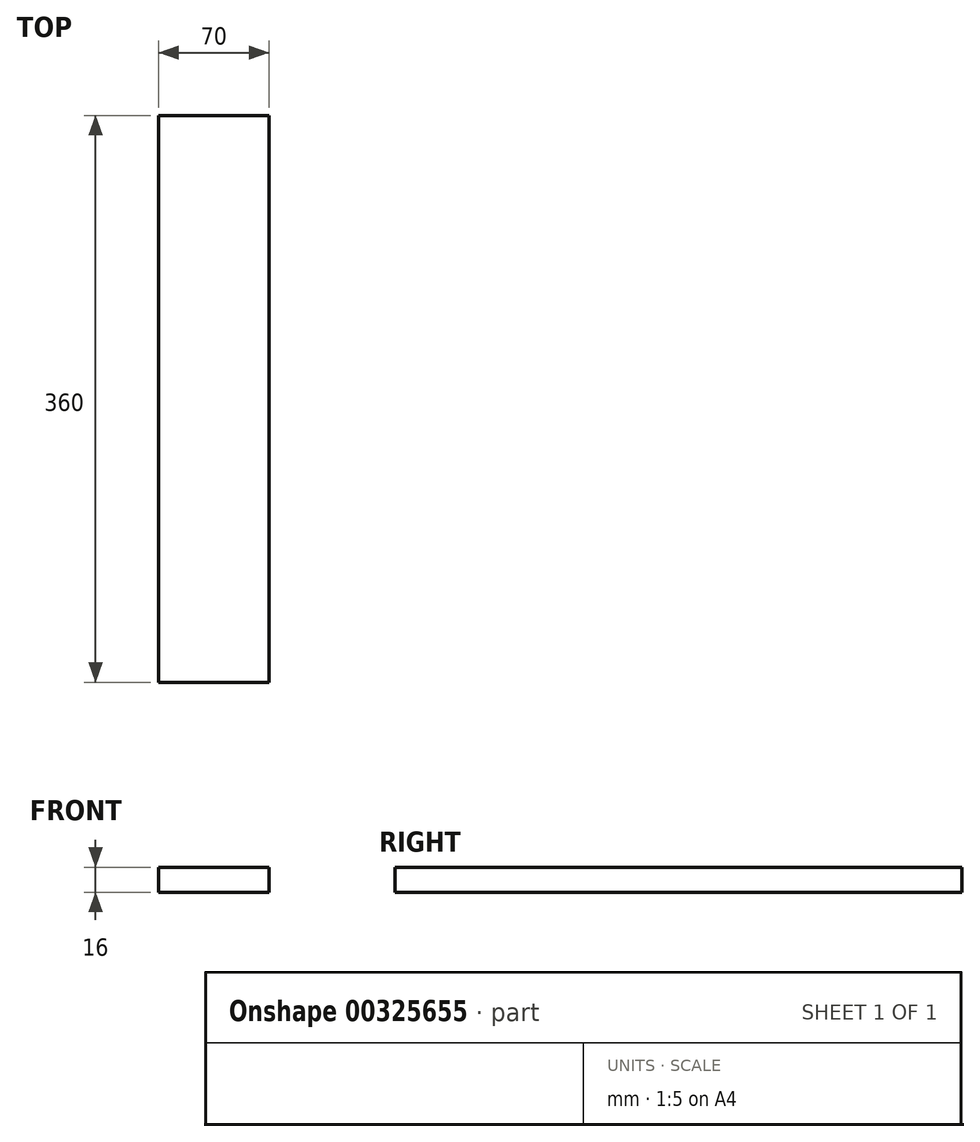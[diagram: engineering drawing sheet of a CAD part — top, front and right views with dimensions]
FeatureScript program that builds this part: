
annotation { "Feature Type Name" : "Feature", "Feature Type Description" : "" }
export const myFeature = defineFeature(function(context is Context, id is Id, definition is map)
    precondition{}
    {
        {
            var Q0;
            Q0=qCreatedBy(makeId("Front.planeOp"),FACE);
            var sketch = newSketch(context, id + "F0", { "sketchPlane" : qUnion([Q0])});
            skLineSegment(sketch, "E0.bottom", {"start": v(0, 0) * mm, "end": v(70, 0) * mm});
            skLineSegment(sketch, "E0.top", {"start": v(0, 16) * mm, "end": v(70, 16) * mm});
            skLineSegment(sketch, "E0.left", {"start": v(0, 0) * mm, "end": v(0, 16) * mm});
            skLineSegment(sketch, "E0.right", {"start": v(70, 0) * mm, "end": v(70, 16) * mm});
            skSolve(sketch);
        }
        {
            var Q0;
            Q0=makeQuery(id+"F0.imprint","IMPRINT",FACE,{"disambiguationData":[TD([[makeQuery(id+"F0.imprint","IMPRINT",EDGE,{"derivedFrom":sQuery(id+"F0.wireOp",EDGE,"E0.bottom")}),1.0]])]});
            extrude(context, id + "F1", {"entities" : qUnion([Q0]), "depth" : 360 * mm});
        }
    });
